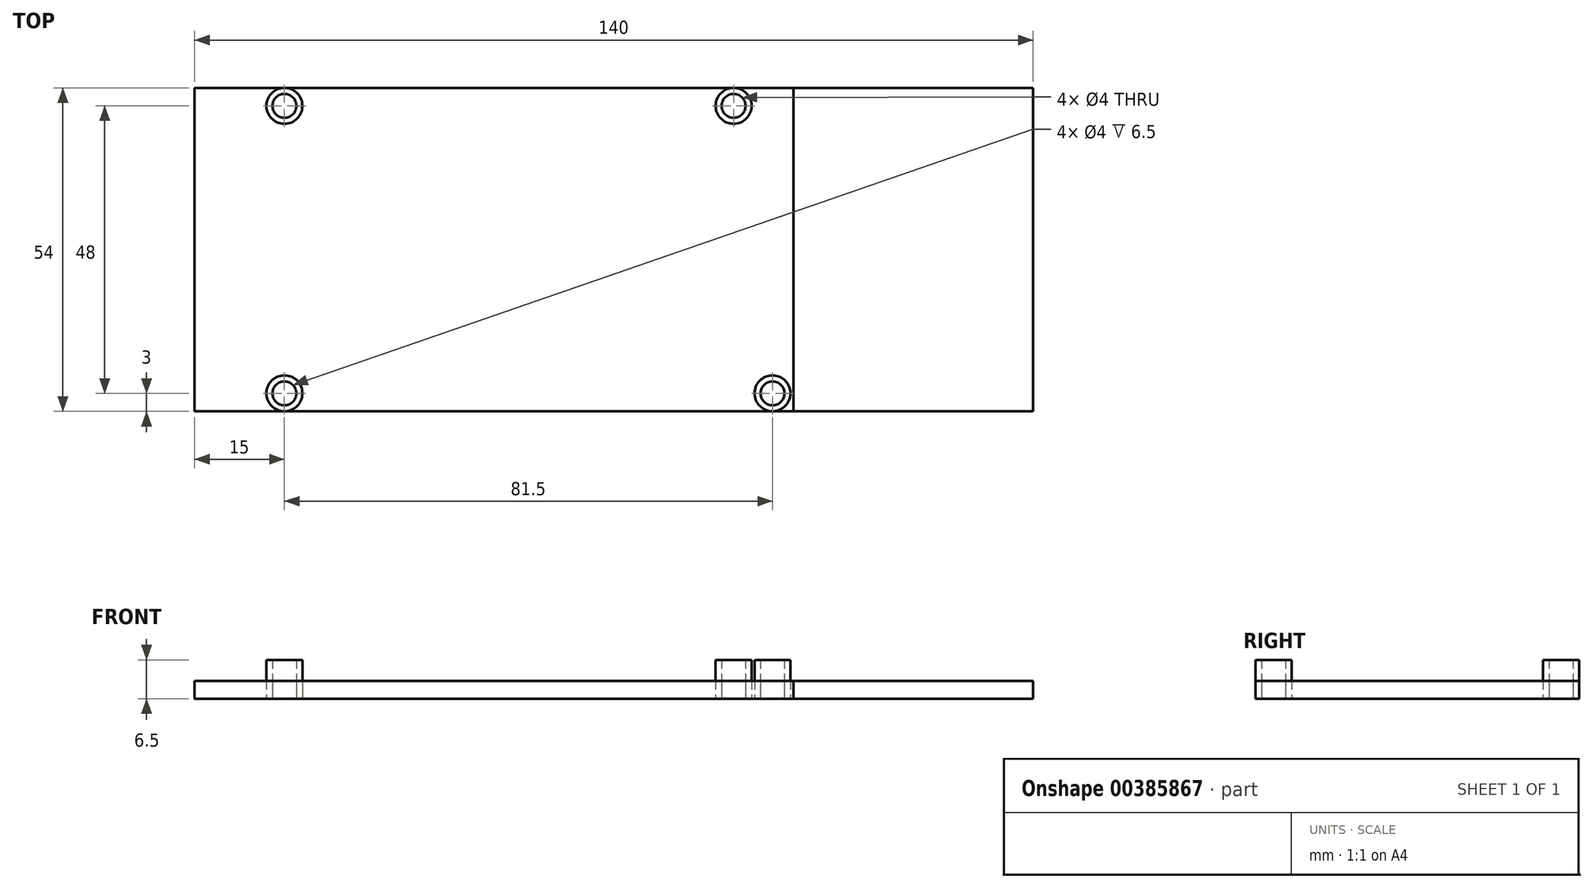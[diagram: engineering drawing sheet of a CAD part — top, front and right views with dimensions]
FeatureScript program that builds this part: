
annotation { "Feature Type Name" : "Feature", "Feature Type Description" : "" }
export const myFeature = defineFeature(function(context is Context, id is Id, definition is map)
    precondition{}
    {
        {
            var Q0;
            Q0=qCreatedBy(makeId("Top.planeOp"),FACE);
            var sketch = newSketch(context, id + "F0", { "sketchPlane" : qUnion([Q0])});
            skLineSegment(sketch, "E0.bottom", {"start": v(-50, 27) * mm, "end": v(50, 27) * mm});
            skLineSegment(sketch, "E0.top", {"start": v(-50, -27) * mm, "end": v(50, -27) * mm});
            skLineSegment(sketch, "E0.left", {"start": v(-50, 27) * mm, "end": v(-50, -27) * mm});
            skLineSegment(sketch, "E0.right", {"start": v(50, 27) * mm, "end": v(50, -27) * mm});
            skPoint(sketch, "E0.middle", {"position": v(0, 0) * mm});
            skPoint(sketch, "E1", {"position": v(-35, 24) * mm});
            skPoint(sketch, "E2", {"position": v(-35, -24) * mm});
            skPoint(sketch, "E3", {"position": v(46.5, -24) * mm});
            skPoint(sketch, "E4", {"position": v(40, 24) * mm});
            skCircle(sketch, "E5", {"center": v(-35, 24) * mm, "radius": 2 * mm});
            skCircle(sketch, "E6", {"center": v(-35, -24) * mm, "radius": 2 * mm});
            skCircle(sketch, "E7", {"center": v(46.5, -24) * mm, "radius": 2 * mm});
            skCircle(sketch, "E8", {"center": v(40, 24) * mm, "radius": 2 * mm});
            skCircle(sketch, "E9", {"center": v(-35, -24) * mm, "radius": 3 * mm});
            skCircle(sketch, "E10", {"center": v(40, 24) * mm, "radius": 3 * mm});
            skCircle(sketch, "E11", {"center": v(46.5, -24) * mm, "radius": 3 * mm});
            skCircle(sketch, "E12", {"center": v(-35, 24) * mm, "radius": 3 * mm});
            skLineSegment(sketch, "E13", {"start": v(90, 27) * mm, "end": v(90, -27) * mm});
            skLineSegment(sketch, "E14", {"start": v(50, -27) * mm, "end": v(90, -27) * mm});
            skLineSegment(sketch, "E15", {"start": v(50, 27) * mm, "end": v(90, 27) * mm});
            skSolve(sketch);
        }
        {
            var Q0;
            Q0=makeQuery(id+"F0.imprint","IMPRINT",FACE,{"disambiguationData":[TD([[makeQuery(id+"F0.imprint","IMPRINT",EDGE,{"derivedFrom":sQuery(id+"F0.wireOp",EDGE,"E6")}),-1.0]])]});
            var Q1;
            Q1=makeQuery(id+"F0.imprint","IMPRINT",FACE,{"disambiguationData":[TD([[makeQuery(id+"F0.imprint","IMPRINT",EDGE,{"derivedFrom":sQuery(id+"F0.wireOp",EDGE,"E5")}),-1.0]])]});
            var Q2;
            Q2=makeQuery(id+"F0.imprint","IMPRINT",FACE,{"disambiguationData":[TD([[makeQuery(id+"F0.imprint","IMPRINT",EDGE,{"derivedFrom":sQuery(id+"F0.wireOp",EDGE,"E8")}),-1.0]])]});
            var Q3;
            Q3=makeQuery(id+"F0.imprint","IMPRINT",FACE,{"disambiguationData":[TD([[makeQuery(id+"F0.imprint","IMPRINT",EDGE,{"derivedFrom":sQuery(id+"F0.wireOp",EDGE,"E7")}),-1.0]])]});
            extrude(context, id + "F1", {"entities" : qUnion([Q0, Q1, Q2, Q3]), "depth" : 6.5 * mm});
        }
        {
            var Q0;
            Q0=makeQuery(id+"F0.imprint","IMPRINT",FACE,{"disambiguationData":[TD([[makeQuery(id+"F0.imprint","IMPRINT",EDGE,{"derivedFrom":sQuery(id+"F0.wireOp",EDGE,"E0.right")}),1.0]])]});
            extrude(context, id + "F2", {"entities" : qUnion([Q0]), "depth" : 3 * mm});
        }
        {
            var Q0;
            {var subQ1=sQuery(id+"F0.wireOp",EDGE,"E0.left");Q0=makeQuery(id+"F0.imprint","IMPRINT",FACE,{"disambiguationData":[TD([[makeQuery(id+"F0.imprint","IMPRINT",EDGE,{"derivedFrom":subQ1}),1.0]])]});}
            var Q1;
            Q1=sQuery(id+"F0.wireOp",EDGE,"E0.top");
            var Q2;
            Q2=sQuery(id+"F0.wireOp",EDGE,"E0.left");
            var Q3;
            Q3=sQuery(id+"F0.wireOp",EDGE,"E0.bottom");
            extrude(context, id + "F3", {"entities" : qUnion([Q0]), "bodyType" : ToolBodyType.SURFACE, "surfaceEntities" : qUnion([Q1, Q2, Q3]), "depth" : 3 * mm});
        }
        {
            var Q0;
            Q0=makeQuery(id+"F3.opExtrude","SWEPT_FACE",FACE,{"disambiguationData":[OSD([sQuery(id+"F0.wireOp",EDGE,"E0.top")])]});
            extrude(context, id + "F4", {"entities" : qUnion([Q0]), "oppositeDirection" : true, "depth" : 54 * mm});
        }
        {
            var Q0;
            Q0=sQuery(id+"F0.wireOp",VERTEX,"E4");
            var Q1;
            Q1=sQuery(id+"F0.wireOp",VERTEX,"E3");
            var Q2;
            Q2=sQuery(id+"F0.wireOp",VERTEX,"E2");
            var Q3;
            Q3=sQuery(id+"F0.wireOp",VERTEX,"E1");
            var Q4;
            Q4=makeQuery(id+"F4.opExtrude","SWEPT_BODY",BODY,{"disambiguationData":[OSD([sQuery(id+"F0.wireOp",EDGE,"E0.top")])]});
            hole(context, id + "F5", {"style" : HoleStyle.SIMPLE, "endStyle" : HoleEndStyle.THROUGH, "oppositeDirection" : true, "holeDiameter" : 4 * mm, "isTappedThrough" : true, "tappedDepth" : 12 * mm, "tapClearance" : 3, "startFromSketch" : true, "locations" : qUnion([Q0, Q1, Q2, Q3]), "scope" : qUnion([Q4])});
        }
    });
